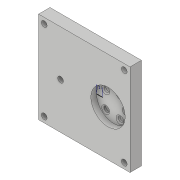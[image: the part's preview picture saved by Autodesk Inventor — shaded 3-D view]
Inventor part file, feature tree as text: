
AUTODESK INVENTOR PART (.ipt)
format: ipt  version: 2019 (Build 230136000, 136)  size: 160,256 bytes
history: native  units: mm
features: sketch x6, extrude x5, fillet x1
ambient origin geometry x8: Origin, YZ Plane, XZ Plane, XY Plane, X Axis, Y Axis, Z Axis, Center Point
bodies: Solid1 (feature_tree)
feature tree (12):
  extrude  "Extrusion1"  Depth=160.0mm
  extrude  "Extrusion2"  Depth=10.0mm
  extrude  "Extrusion3"  Depth=140.0mm
  extrude  "Extrusion4"  Depth=140.0mm
  sketch  "Sketch5"  dims[d9=10.0mm d10=10.0mm d11=10.0mm]
  extrude  "Extrusion5"  Depth=10.0mm
  fillet  "Fillet1"  Radius=10.0mm
  sketch  "Sketch1"  dims[d0=160.0mm d1=160.0mm]
  sketch  "Sketch2"  dims[d2=20.0mm d3=0.0mm d4=10.0mm]
  sketch  "Sketch3"  dims[d5=150.0mm d6=140.0mm]
  sketch  "Sketch4"  dims[d7=140.0mm d8=140.0mm]
  sketch  "Sketch6"  dims[d12=10.0mm d13=80.0mm d14=38.5mm d15=10.0mm d16=80.0mm d17=38.5mm d18=60.0mm d19=0.0mm d20=0.0mm d21=80.0mm d22=38.5mm d23=10.0mm d24=10.0mm d25=0.0mm d26=80.0mm d27=38.5mm d28=60.0mm d29=10.0mm d30=0.0mm d31=10.0mm d32=10.0mm d33=10.0mm d34=10.0mm d35=10.0mm d36=10.0mm d37=5.0mm d38=0.0mm d39=2.0mm]
